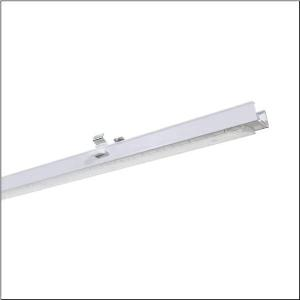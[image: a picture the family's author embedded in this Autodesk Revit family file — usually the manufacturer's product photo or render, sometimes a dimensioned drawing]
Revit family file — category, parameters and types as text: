
# Revit family: trunking_flex_31_51re12mb48b
name_source: partatom
category: Lighting Fixtures
units: mm (PartAtom-declared; Revit-internal decimal feet)

## family parameters
Cut with Voids When Loaded = No
Host = Face
Light Source = No
Part Type = Normal
Room Calculation Point = No
Round Connector Dimension = Use Diameter
Shared = No

## types (1)
- --- (1 x LED, 8000 lm, 50 W, 4000K)
    Apparent Load = 50 VA
    CIE Flux Codes = 65 91 98 99 100
    Color Rendering = 80
    Color Temperature = 4000K
    Default Elevation = 1800 mm
    Description = Trunking Flex 31, luminaire insert, of extruded aluminium section, coated, traffic white (RAL 9016), length: 1.472mm, width: 91mm, height: 53mm, LED rated luminous flux: 8.000lm, light colour: 840, control gear: ON/OFF Multilumen, with system connector: socket, mains connection: 220..240V, AC, 50/60Hz, rated input power: 50W, luminous flux adjustable on luminaire in four steps (4130/5610/6850/8000lm), connected load according to luminous flux setting (25/34/42/50W), primary light control with lens, of plastic, primary optical cover: cover, of PMMA, light emission: direct distribution, protection rating (complete): IP20, insulation class (complete): insulation class I (protective earthing), certification: CE, UKCA, impact resistance: IK02, permissible ambient temperature for indoor applications: -20..+40°C, packaging unit: 1 piece
    Height = 58 mm
    Lamp = 1 x LED
    Lamp Light Flux = 8000 lm
    Lamp Power = 50 W
    Lamp count = 1
    Length = 1472 mm
    Luminous efficacy = 160 lm/W
    Manufacturer = Siteco
    ModVariant = No
    Model = 51RE12MB48B
    Mounting Place = Ceiling
    Mounting Type = Pendant
    Number of Poles = 1
    OnlyDefault = Yes
    Power Factor = 1
    Product Name = Trunking Flex 31
    Product group = luminaire insert
    ProductGroupID = 901
    Protection Class = Protection class I
    Protection Degree = IP 20
    RLX_Detail_Level = 1
    RLX_Emergency_Light_Flux = 0 lm
    RLX_Emergency_Type = 0
    RLX_Emergency_Type_DB = No
    RlxData = <blob elided: 20325 chars, md5=0c4d4972>
    Socket = socket
    Standby Power = 0 W
    System Light Flux = 8000 lm
    System Power = 50 W
    Type Comments = factory setting: luminous flux: 100 % | (ON | ON) | 300 mA
    Type Image = l_1266702.jpg
    URL = http://relux.com
    VarID = @adj_001273
    Voltage = 0 V
    Weight = 0.00 kg
    Width = 65 mm

## geometry (parser evidence)
native form markers: Blend x4, Sweep x11
no freeform markers — native parametric forms only
